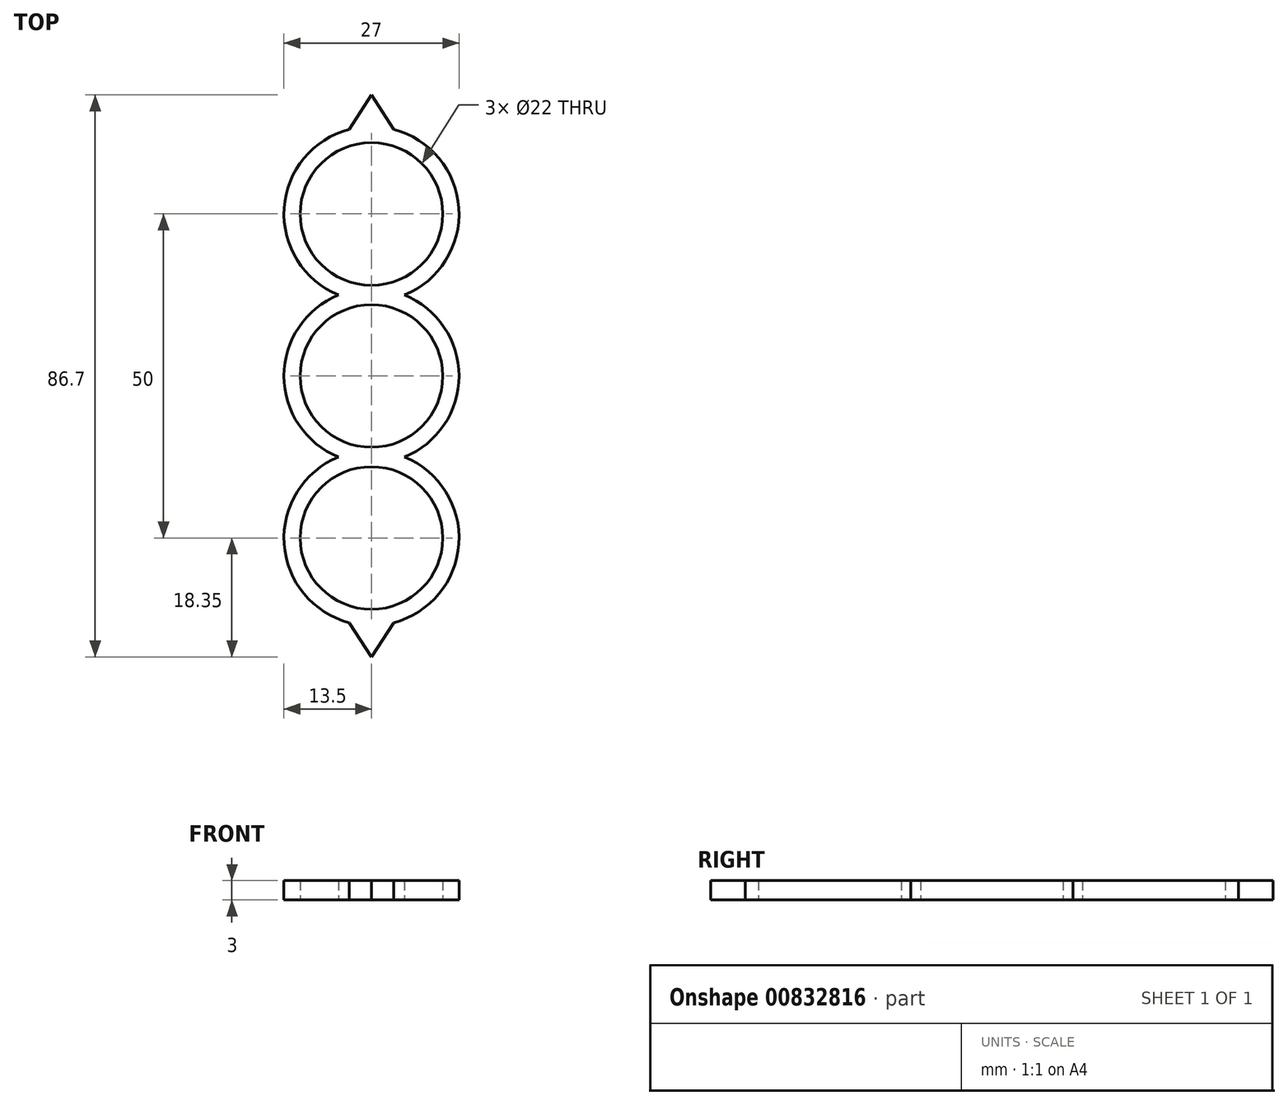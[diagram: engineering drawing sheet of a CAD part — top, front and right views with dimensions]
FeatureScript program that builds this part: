
annotation { "Feature Type Name" : "Feature", "Feature Type Description" : "" }
export const myFeature = defineFeature(function(context is Context, id is Id, definition is map)
    precondition{}
    {
        {
            var Q0;
            Q0=qCreatedBy(makeId("Top.planeOp"),FACE);
            var sketch = newSketch(context, id + "F0", { "sketchPlane" : qUnion([Q0])});
            skCircle(sketch, "E0", {"center": v(0, 0) * mm, "radius": 11 * mm});
            skArc(sketch, "E1", {"start": v(-5.1, 12.5) * mm, "mid": v(-13.5, 0) * mm, "end": v(-5.1, -12.5) * mm});
            skCircle(sketch, "E2", {"center": v(0, 25) * mm, "radius": 11 * mm});
            skArc(sketch, "E3", {"start": v(5.1, 12.5) * mm, "mid": v(13.47, 25.9) * mm, "end": v(3.4, 38.06) * mm});
            skCircle(sketch, "E4.MirrorC", {"center": v(0, -25) * mm, "radius": 11 * mm});
            skArc(sketch, "E5.MirrorC", {"start": v(5.1, -12.5) * mm, "mid": v(13.47, -25.9) * mm, "end": v(3.4, -38.06) * mm});
            skArc(sketch, "E6.trimOffspring", {"start": v(5.1, -12.5) * mm, "mid": v(13.5, 0) * mm, "end": v(5.1, 12.5) * mm});
            skLineSegment(sketch, "E7", {"start": v(0, 43.35) * mm, "end": v(-3.4, 38.06) * mm});
            skLineSegment(sketch, "E8.MirrorCS", {"start": v(0, 43.35) * mm, "end": v(3.4, 38.06) * mm});
            skLineSegment(sketch, "E9.MirrorCS", {"start": v(0, -43.35) * mm, "end": v(-3.4, -38.06) * mm});
            skLineSegment(sketch, "E10.MirrorCS", {"start": v(0, -43.35) * mm, "end": v(3.4, -38.06) * mm});
            skArc(sketch, "E11.trimOffspring", {"start": v(-3.4, 38.06) * mm, "mid": v(-13.47, 25.9) * mm, "end": v(-5.1, 12.5) * mm});
            skArc(sketch, "E12.trimOffspring", {"start": v(-3.4, -38.06) * mm, "mid": v(-13.47, -25.9) * mm, "end": v(-5.1, -12.5) * mm});
            skSolve(sketch);
        }
        {
            var Q0;
            Q0 = qSketchRegion(id + "F0", true);
            extrude(context, id + "F1", {"entities" : qUnion([Q0]), "depth" : 3 * mm, "offsetDistance" : 25 * mm});
        }
    });
